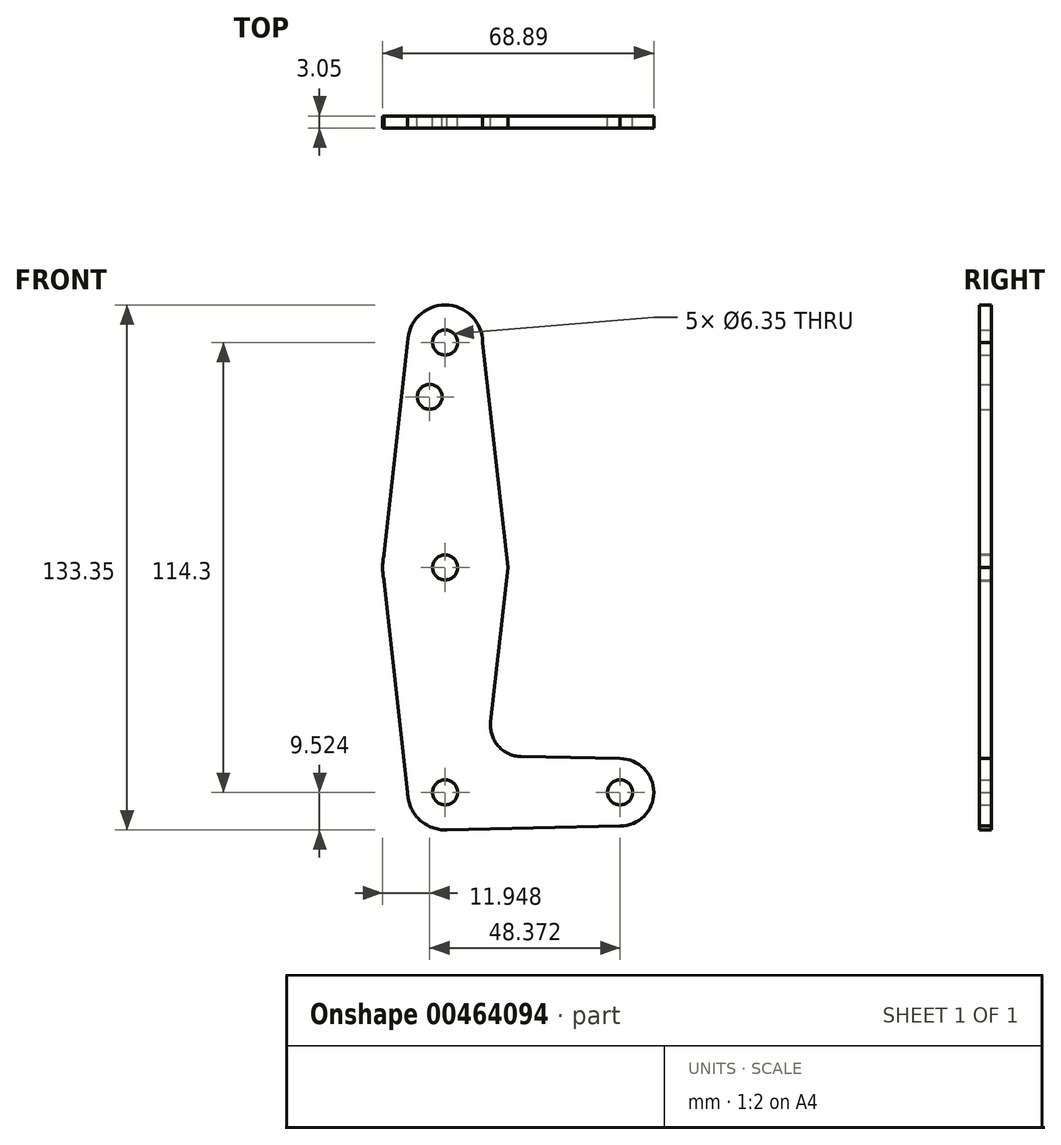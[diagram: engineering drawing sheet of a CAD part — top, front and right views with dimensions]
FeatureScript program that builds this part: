
annotation { "Feature Type Name" : "Feature", "Feature Type Description" : "" }
export const myFeature = defineFeature(function(context is Context, id is Id, definition is map)
    precondition{}
    {
        {
            var Q0;
            Q0=qCreatedBy(makeId("Front.planeOp"),FACE);
            var sketch = newSketch(context, id + "F0", { "sketchPlane" : qUnion([Q0])});
            skLineSegment(sketch, "E0", {"start": v(0, 76.06) * mm, "end": v(0, -38.24) * mm});
            skCircle(sketch, "E1", {"center": v(0, 76.06) * mm, "radius": 9.53 * mm});
            skCircle(sketch, "E2", {"center": v(0, -38.24) * mm, "radius": 9.53 * mm});
            skCircle(sketch, "E3", {"center": v(0, 18.91) * mm, "radius": 15.88 * mm});
            skCircle(sketch, "E4", {"center": v(44.45, -38.24) * mm, "radius": 8.57 * mm});
            skLineSegment(sketch, "E5", {"start": v(-9.52, 76.06) * mm, "end": v(-15.88, 18.91) * mm});
            skLineSegment(sketch, "E6", {"start": v(9.52, 76.06) * mm, "end": v(15.98, 18.91) * mm});
            skLineSegment(sketch, "E7", {"start": v(-15.88, 18.91) * mm, "end": v(-9.52, -38.24) * mm});
            skLineSegment(sketch, "E8", {"start": v(15.98, 18.91) * mm, "end": v(11.55, -20.28) * mm});
            skLineSegment(sketch, "E9", {"start": v(19.28, -29.12) * mm, "end": v(44.45, -29.66) * mm});
            skCircle(sketch, "E10", {"center": v(0, 76.06) * mm, "radius": 3.18 * mm});
            skCircle(sketch, "E11", {"center": v(0, 18.91) * mm, "radius": 3.18 * mm});
            skCircle(sketch, "E12", {"center": v(44.45, -38.24) * mm, "radius": 3.18 * mm});
            skCircle(sketch, "E13", {"center": v(-3.92, 62.27) * mm, "radius": 3.18 * mm});
            skPoint(sketch, "E14.newPointB", {"position": v(0, -28.71) * mm});
            skArc(sketch, "E14.filletArc", {"start": v(11.55, -20.28) * mm, "mid": v(13.47, -26.4) * mm, "end": v(19.28, -29.12) * mm});
            skLineSegment(sketch, "E15", {"start": v(0, -47.76) * mm, "end": v(44.45, -46.8) * mm});
            skCircle(sketch, "E16", {"center": v(0, -38.24) * mm, "radius": 3.18 * mm});
            skSolve(sketch);
        }
        {
            var Q0;
            Q0 = qSketchRegion(id + "F0", true);
            extrude(context, id + "F1", {"entities" : qUnion([Q0]), "depth" : 3.05 * mm});
        }
    });
